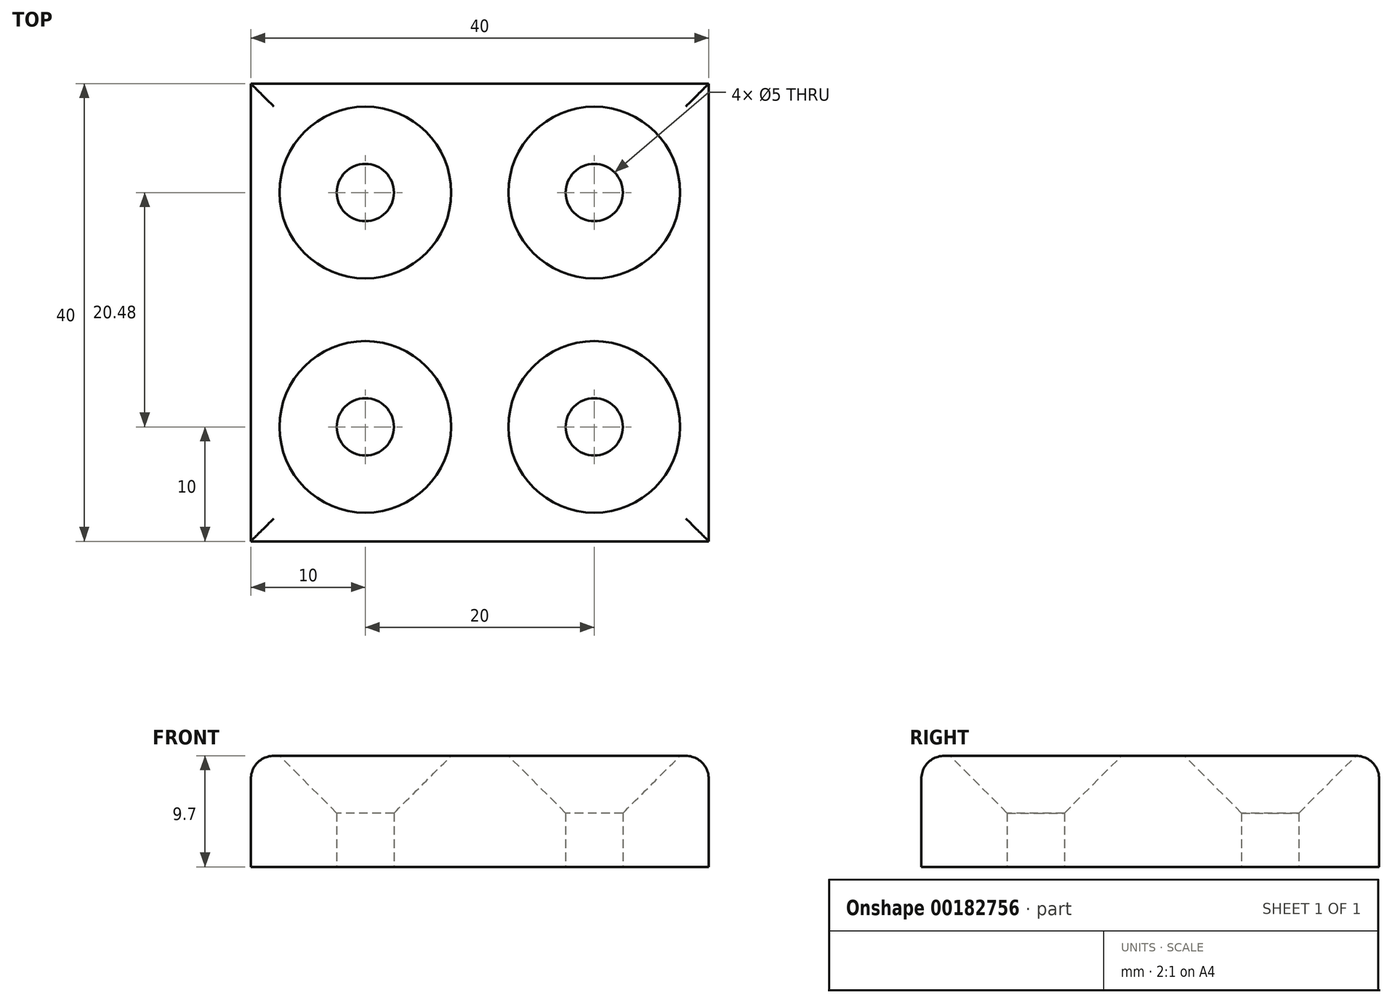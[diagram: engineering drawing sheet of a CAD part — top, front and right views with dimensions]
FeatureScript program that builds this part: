
annotation { "Feature Type Name" : "Feature", "Feature Type Description" : "" }
export const myFeature = defineFeature(function(context is Context, id is Id, definition is map)
    precondition{}
    {
        {
            var Q0;
            Q0=qCreatedBy(makeId("Top.planeOp"),FACE);
            var sketch = newSketch(context, id + "F0", { "sketchPlane" : qUnion([Q0])});
            skLineSegment(sketch, "E0.bottom", {"start": v(-20, -20) * mm, "end": v(20, -20) * mm});
            skLineSegment(sketch, "E0.top", {"start": v(-20, 20) * mm, "end": v(20, 20) * mm});
            skLineSegment(sketch, "E0.left", {"start": v(-20, -20) * mm, "end": v(-20, 20) * mm});
            skLineSegment(sketch, "E0.right", {"start": v(20, -20) * mm, "end": v(20, 20) * mm});
            skPoint(sketch, "E0.middle", {"position": v(0, 0) * mm});
            skLineSegment(sketch, "E1", {"start": v(0, -20) * mm, "end": v(-10, -20) * mm});
            skLineSegment(sketch, "E2", {"start": v(-10, 20) * mm, "end": v(10, 20) * mm});
            skLineSegment(sketch, "E3", {"start": v(-20, 20) * mm, "end": v(-20, 10.48) * mm});
            skCircle(sketch, "E4", {"center": v(-10, 10.48) * mm, "radius": 2.5 * mm});
            skCircle(sketch, "E5", {"center": v(10, 10.48) * mm, "radius": 2.5 * mm});
            skCircle(sketch, "E6", {"center": v(10, -10) * mm, "radius": 2.5 * mm});
            skCircle(sketch, "E7", {"center": v(-10, -10) * mm, "radius": 2.5 * mm});
            skPoint(sketch, "E8.orphan", {"position": v(-20, 0) * mm});
            skPoint(sketch, "E9.end.orphan", {"position": v(20, 0) * mm});
            skPoint(sketch, "E10.orphan", {"position": v(20, -10) * mm});
            skPoint(sketch, "E11.end.orphan", {"position": v(0, -10) * mm});
            skPoint(sketch, "E12.end.orphan", {"position": v(0, 20) * mm});
            skSolve(sketch);
        }
        {
            var Q0;
            Q0 = qSketchRegion(id + "F0", true);
            extrude(context, id + "F1", {"entities" : qUnion([Q0]), "depth" : 9.7 * mm});
        }
        {
            var Q0;
            Q0=makeQuery(id+"F1.opExtrude","CAP_EDGE",EDGE,{"disambiguationData":[OSD([sQuery(id+"F0.wireOp",EDGE,"E4")])],"isStart":false});
            var Q1;
            Q1=makeQuery(id+"F1.opExtrude","CAP_EDGE",EDGE,{"disambiguationData":[OSD([sQuery(id+"F0.wireOp",EDGE,"E5")])],"isStart":false});
            var Q2;
            Q2=makeQuery(id+"F1.opExtrude","CAP_EDGE",EDGE,{"disambiguationData":[OSD([sQuery(id+"F0.wireOp",EDGE,"E6")])],"isStart":false});
            var Q3;
            Q3=makeQuery(id+"F1.opExtrude","CAP_EDGE",EDGE,{"disambiguationData":[OSD([sQuery(id+"F0.wireOp",EDGE,"E7")])],"isStart":false});
            chamfer(context, id + "F2", {"entities" : qUnion([Q0, Q1, Q2, Q3]), "width" : 5 * mm, "tangentPropagation" : true});
        }
        {
            var Q0;
            Q0=makeQuery(id+"F1.opExtrude","CAP_EDGE",EDGE,{"disambiguationData":[OSD([sQuery(id+"F0.wireOp",EDGE,"E0.bottom"),sQuery(id+"F0.wireOp",EDGE,"E1")])],"isStart":false});
            var Q1;
            Q1=makeQuery(id+"F1.opExtrude","CAP_EDGE",EDGE,{"disambiguationData":[OSD([sQuery(id+"F0.wireOp",EDGE,"E0.right")])],"isStart":false});
            var Q2;
            Q2=makeQuery(id+"F1.opExtrude","CAP_EDGE",EDGE,{"disambiguationData":[OSD([sQuery(id+"F0.wireOp",EDGE,"E0.top"),sQuery(id+"F0.wireOp",EDGE,"E2")])],"isStart":false});
            var Q3;
            Q3=makeQuery(id+"F1.opExtrude","CAP_EDGE",EDGE,{"disambiguationData":[OSD([sQuery(id+"F0.wireOp",EDGE,"E0.left"),sQuery(id+"F0.wireOp",EDGE,"E3")])],"isStart":false});
            fillet(context, id + "F3", {"entities" : qUnion([Q0, Q1, Q2, Q3]), "radius" : 2 * mm, "tangentPropagation" : true, "allowEdgeOverflow" : false});
        }
    });
